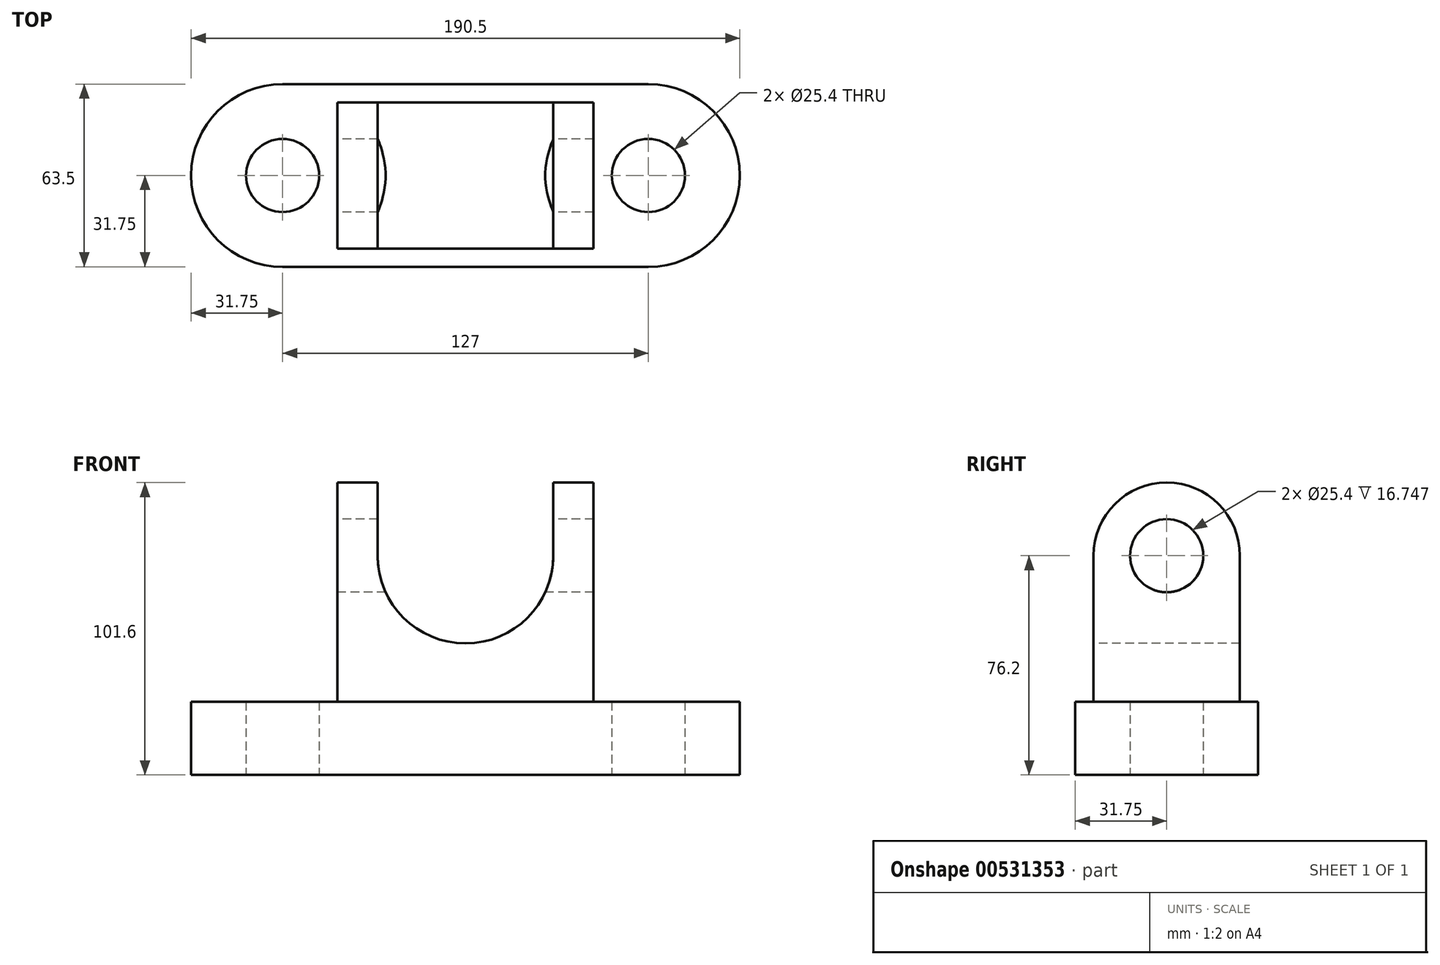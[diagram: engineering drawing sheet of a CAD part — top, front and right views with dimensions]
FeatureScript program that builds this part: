
annotation { "Feature Type Name" : "Feature", "Feature Type Description" : "" }
export const myFeature = defineFeature(function(context is Context, id is Id, definition is map)
    precondition{}
    {
        {
            var Q0;
            Q0=qCreatedBy(makeId("Top.planeOp"),FACE);
            var sketch = newSketch(context, id + "F0", { "sketchPlane" : qUnion([Q0])});
            skLineSegment(sketch, "E0.bottom", {"start": v(63.5, -31.75) * mm, "end": v(-63.5, -31.75) * mm});
            skLineSegment(sketch, "E0.top", {"start": v(63.5, 31.75) * mm, "end": v(-63.5, 31.75) * mm});
            skPoint(sketch, "E0.middle", {"position": v(0, 0) * mm});
            skArc(sketch, "E1", {"start": v(-63.5, 31.75) * mm, "mid": v(-95.25, 0) * mm, "end": v(-63.5, -31.75) * mm});
            skArc(sketch, "E2", {"start": v(63.5, -31.75) * mm, "mid": v(95.25, 0) * mm, "end": v(63.5, 31.75) * mm});
            skCircle(sketch, "E3", {"center": v(-63.5, 0) * mm, "radius": 12.7 * mm});
            skPoint(sketch, "E4.endSnap0", {"position": v(0, -31.75) * mm});
            skCircle(sketch, "E5", {"center": v(63.5, 0) * mm, "radius": 12.7 * mm});
            skSolve(sketch);
        }
        {
            var Q0;
            Q0=makeQuery(id+"F0.imprint","IMPRINT",FACE,{"disambiguationData":[TD([[makeQuery(id+"F0.imprint","IMPRINT",EDGE,{"derivedFrom":sQuery(id+"F0.wireOp",EDGE,"E0.bottom")}),-1.0]])]});
            extrude(context, id + "F1", {"entities" : qUnion([Q0]), "depth" : 25.4 * mm, "offsetDistance" : 25.4 * mm});
        }
        {
            var Q0;
            Q0=makeQuery(id+"F1.opExtrude","CAP_FACE",FACE,{"disambiguationData":[OSD([sQuery(id+"F0.wireOp",EDGE,"E0.bottom"),sQuery(id+"F0.wireOp",EDGE,"E0.top"),sQuery(id+"F0.wireOp",EDGE,"E1"),sQuery(id+"F0.wireOp",EDGE,"E2"),sQuery(id+"F0.wireOp",EDGE,"E3"),sQuery(id+"F0.wireOp",EDGE,"E5")])],"isStart":false});
            var sketch = newSketch(context, id + "F2", { "sketchPlane" : qUnion([Q0])});
            skLineSegment(sketch, "E6.bottom", {"start": v(44.45, -25.4) * mm, "end": v(-44.45, -25.4) * mm});
            skLineSegment(sketch, "E6.top", {"start": v(44.45, 25.4) * mm, "end": v(-44.45, 25.4) * mm});
            skLineSegment(sketch, "E6.left", {"start": v(44.45, -25.4) * mm, "end": v(44.45, 25.4) * mm});
            skLineSegment(sketch, "E6.right", {"start": v(-44.45, -25.4) * mm, "end": v(-44.45, 25.4) * mm});
            skPoint(sketch, "E6.middle", {"position": v(0, 0) * mm});
            skSolve(sketch);
        }
        {
            var Q0;
            Q0=makeQuery(id+"F2.imprint","IMPRINT",FACE,{"disambiguationData":[TD([[makeQuery(id+"F2.imprint","IMPRINT",EDGE,{"derivedFrom":sQuery(id+"F2.wireOp",EDGE,"E6.bottom")}),-1.0]])]});
            extrude(context, id + "F3", {"entities" : qUnion([Q0]), "operationType" : NewBodyOperationType.ADD, "depth" : 50.8 * mm, "offsetDistance" : 25.4 * mm});
        }
        {
            var Q0;
            Q0=makeQuery(id+"F3.opExtrude","SWEPT_FACE",FACE,{"disambiguationData":[OSD([sQuery(id+"F2.wireOp",EDGE,"E6.right")])]});
            var sketch = newSketch(context, id + "F4", { "sketchPlane" : qUnion([Q0])});
            skArc(sketch, "E7", {"start": v(25.4, 76.2) * mm, "mid": v(0, 101.6) * mm, "end": v(-25.4, 76.2) * mm});
            skLineSegment(sketch, "E8", {"start": v(-25.4, 76.2) * mm, "end": v(25.4, 76.2) * mm});
            skSolve(sketch);
        }
        {
            var Q0;
            Q0=makeQuery(id+"F4.imprint","IMPRINT",FACE,{"disambiguationData":[TD([[makeQuery(id+"F4.imprint","IMPRINT",EDGE,{"derivedFrom":sQuery(id+"F4.wireOp",EDGE,"E7")}),1.0]])]});
            extrude(context, id + "F5", {"entities" : qUnion([Q0]), "operationType" : NewBodyOperationType.ADD, "oppositeDirection" : true, "depth" : 88.9 * mm, "offsetDistance" : 25.4 * mm});
        }
        {
            var Q0;
            Q0=makeQuery(id+"F3.opExtrude","SWEPT_FACE",FACE,{"disambiguationData":[OSD([sQuery(id+"F2.wireOp",EDGE,"E6.bottom")])]});
            var sketch = newSketch(context, id + "F6", { "sketchPlane" : qUnion([Q0])});
            skLineSegment(sketch, "E9.top", {"start": v(30.48, 114.3) * mm, "end": v(-30.48, 114.3) * mm});
            skLineSegment(sketch, "E9.left", {"start": v(30.48, 76.2) * mm, "end": v(30.48, 114.3) * mm});
            skLineSegment(sketch, "E9.right", {"start": v(-30.48, 76.2) * mm, "end": v(-30.48, 114.3) * mm});
            skPoint(sketch, "E9.middle", {"position": v(0, 76.2) * mm});
            skCircle(sketch, "E10", {"center": v(0, 76.2) * mm, "radius": 30.48 * mm});
            skPoint(sketch, "E9.bottom.start.orphan", {"position": v(30.48, 38.1) * mm});
            skPoint(sketch, "E11.orphan", {"position": v(-30.48, 38.1) * mm});
            skSolve(sketch);
        }
        {
            var Q0;
            {var subQ0=sQuery(id+"F6.wireOp",EDGE,"E9.bottom");Q0=makeQuery(id+"F6.imprint","IMPRINT",FACE,{"disambiguationData":[TD([[makeQuery(id+"F6.imprint","IMPRINT",EDGE,{"derivedFrom":subQ0}),-1.0]])]});}
            var Q1;
            {var subQ0=sQuery(id+"F6.wireOp",EDGE,"E10");var subQ1=sQuery(id+"F2.wireOp",EDGE,"E6.bottom");var subQ2=makeQuery(id+"F5.boolean.opBoolean","MERGE",EDGE,{"derivedFrom":[makeQuery(id+"F3.opExtrude","CAP_EDGE",EDGE,{"disambiguationData":[OSD([subQ1])],"isStart":false}),makeQuery(id+"F5.opExtrude","SWEPT_EDGE",EDGE,{"disambiguationData":[OSD([subQ1,sQuery(id+"F2.wireOp",EDGE,"E6.right"),sQuery(id+"F4.wireOp",EDGE,"E7"),sQuery(id+"F4.wireOp",EDGE,"E8")])]})]});var subQ3=makeQuery(id+"F6.imprint","INTERSECT",VERTEX,{"derivedFrom":[subQ2,sQuery(id+"F6.wireOp",EDGE,"E9.left"),subQ0]});Q1=makeQuery(id+"F6.imprint","IMPRINT",FACE,{"disambiguationData":[TD([[makeQuery(id+"F6.imprint","IMPRINT",EDGE,{"disambiguationData":[TD([[subQ3,-1.0]])],"derivedFrom":subQ0}),1.0]])]});}
            var Q2;
            {var subQ0=sQuery(id+"F6.wireOp",EDGE,"E10");var subQ1=sQuery(id+"F2.wireOp",EDGE,"E6.bottom");var subQ2=makeQuery(id+"F5.boolean.opBoolean","MERGE",EDGE,{"derivedFrom":[makeQuery(id+"F3.opExtrude","CAP_EDGE",EDGE,{"disambiguationData":[OSD([subQ1])],"isStart":false}),makeQuery(id+"F5.opExtrude","SWEPT_EDGE",EDGE,{"disambiguationData":[OSD([subQ1,sQuery(id+"F2.wireOp",EDGE,"E6.right"),sQuery(id+"F4.wireOp",EDGE,"E7"),sQuery(id+"F4.wireOp",EDGE,"E8")])]})]});var subQ3=makeQuery(id+"F6.imprint","INTERSECT",VERTEX,{"derivedFrom":[subQ2,sQuery(id+"F6.wireOp",EDGE,"E9.left"),subQ0]});Q2=makeQuery(id+"F6.imprint","IMPRINT",FACE,{"disambiguationData":[TD([[makeQuery(id+"F6.imprint","IMPRINT",EDGE,{"disambiguationData":[TD([[subQ3,1.0]])],"derivedFrom":subQ0}),1.0]])]});}
            var Q3;
            Q3=makeQuery(id+"F6.imprint","IMPRINT",FACE,{"disambiguationData":[TD([[makeQuery(id+"F6.imprint","IMPRINT",EDGE,{"derivedFrom":sQuery(id+"F6.wireOp",EDGE,"E9.top")}),1.0]])]});
            extrude(context, id + "F7", {"entities" : qUnion([Q0, Q1, Q2, Q3]), "operationType" : NewBodyOperationType.REMOVE, "oppositeDirection" : true, "depth" : 75.95 * mm, "offsetDistance" : 25.4 * mm});
        }
        {
            var Q0;
            Q0=makeQuery(id+"F5.boolean.opBoolean","MERGE",FACE,{"derivedFrom":[makeQuery(id+"F3.opExtrude","SWEPT_FACE",FACE,{"disambiguationData":[OSD([sQuery(id+"F2.wireOp",EDGE,"E6.right")])]}),makeQuery(id+"F5.opExtrude","CAP_FACE",FACE,{"disambiguationData":[OSD([sQuery(id+"F4.wireOp",EDGE,"E7"),sQuery(id+"F4.wireOp",EDGE,"E8")])],"isStart":true})]});
            var sketch = newSketch(context, id + "F8", { "sketchPlane" : qUnion([Q0])});
            skCircle(sketch, "E12", {"center": v(0, 76.2) * mm, "radius": 12.7 * mm});
            skSolve(sketch);
        }
        {
            var Q0;
            Q0=makeQuery(id+"F8.imprint","IMPRINT",FACE,{"disambiguationData":[TD([[makeQuery(id+"F8.imprint","IMPRINT",EDGE,{"derivedFrom":sQuery(id+"F8.wireOp",EDGE,"E12")}),1.0]])]});
            extrude(context, id + "F9", {"entities" : qUnion([Q0]), "operationType" : NewBodyOperationType.REMOVE, "oppositeDirection" : true, "depth" : 112.78 * mm, "offsetDistance" : 25.4 * mm});
        }
    });
